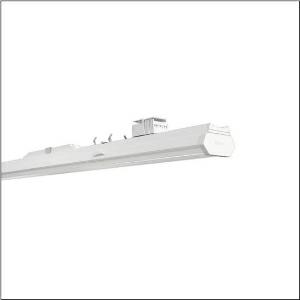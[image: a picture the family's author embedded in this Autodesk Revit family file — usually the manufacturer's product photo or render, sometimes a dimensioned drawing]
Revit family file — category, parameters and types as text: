
# Revit family: licross_r__11_protected_mo_51tp12cn48xfd_cafa
name_source: partatom
category: Lighting Fixtures
units: mm (PartAtom-declared; Revit-internal decimal feet)

## family parameters
Cut with Voids When Loaded = No
Host = Face
Light Source = No
Part Type = Normal
Room Calculation Point = No
Round Connector Dimension = Use Diameter
Shared = No

## types (1)
- --- (1 x LED, 3310 lm, 21.7 W, 4000K)
    Apparent Load = 22 VA
    CIE Flux Codes = 73 92 98 99 100
    Color Rendering = 80
    Color Temperature = 4000K
    Default Elevation = 1800 mm
    Description = Licross® 11 Protected MOluminaire insert, length: 1.500mm, width: 90mm, height: 101mm, LED rated luminous flux: 8.180lm, light colour: 840, control gear: ON/OFF Multilumen, CLOi, control gear: ECG Multilumen, with plug, 6-pole, with phase selection, mains connection: 220..240V, AC/DC, 0/50..60Hz, without changeover relay, for emergency light function, for central battery installations according to DIN EN 60598-2-22, halogen-free wiring, primary optical cover: cover, of PMMA, light emission: direct with ceiling illumination distribution, protection rating (complete): IP64, insulation class (complete): insulation class I (protective earthing), certification: CE, ENEC, VDE, protection symbol: D if used in an environment without relevant dust loads with corresponding accessories, permissible ambient temperature for indoor applications: -35..+40°C, standard: EN 60598-2-22, reducing of maximum allowable ambient temperature of 5°C with ceiling mounting, corresponds to IFS (International Featured Standards) requirements for safety and quality in the food industry, packaging unit: 1 piece
    Height = 92 mm
    Lamp = 1 x LED
    Lamp Light Flux = 3310 lm
    Lamp Power = 21.7 W
    Lamp count = 1
    Length = 1500 mm
    Luminous efficacy = 153 lm/W
    Manufacturer = Siteco
    ModVariant = No
    Model = 51TP12CN48XFD
    Mounting Place = Ceiling
    Mounting Type = Pendant
    Number of Poles = 1
    OnlyDefault = Yes
    Power Factor = 1
    Product Name = Licross® 11 Protected MO
    Product group = luminaire insert
    ProductGroupID = 902
    Protection Class = Protection class I
    Protection Degree = IP 64
    RLX_Detail_Level = 1
    RlxData = <blob elided: 22245 chars, md5=bfbd097e>
    Socket = socket
    Standby Power = 0 W
    System Light Flux = 3310 lm
    System Power = 22 W
    Type Comments = : DC mode (central or group accumulator) initial emergency light level
    Type Image = l_1256148.jpg
    URL = http://relux.com
    VarID = @adj_134707
    Voltage = 0 V
    Weight = 0.00 kg
    Width = 88 mm

## geometry (parser evidence)
native form markers: Blend x4, Sweep x11
no freeform markers — native parametric forms only
